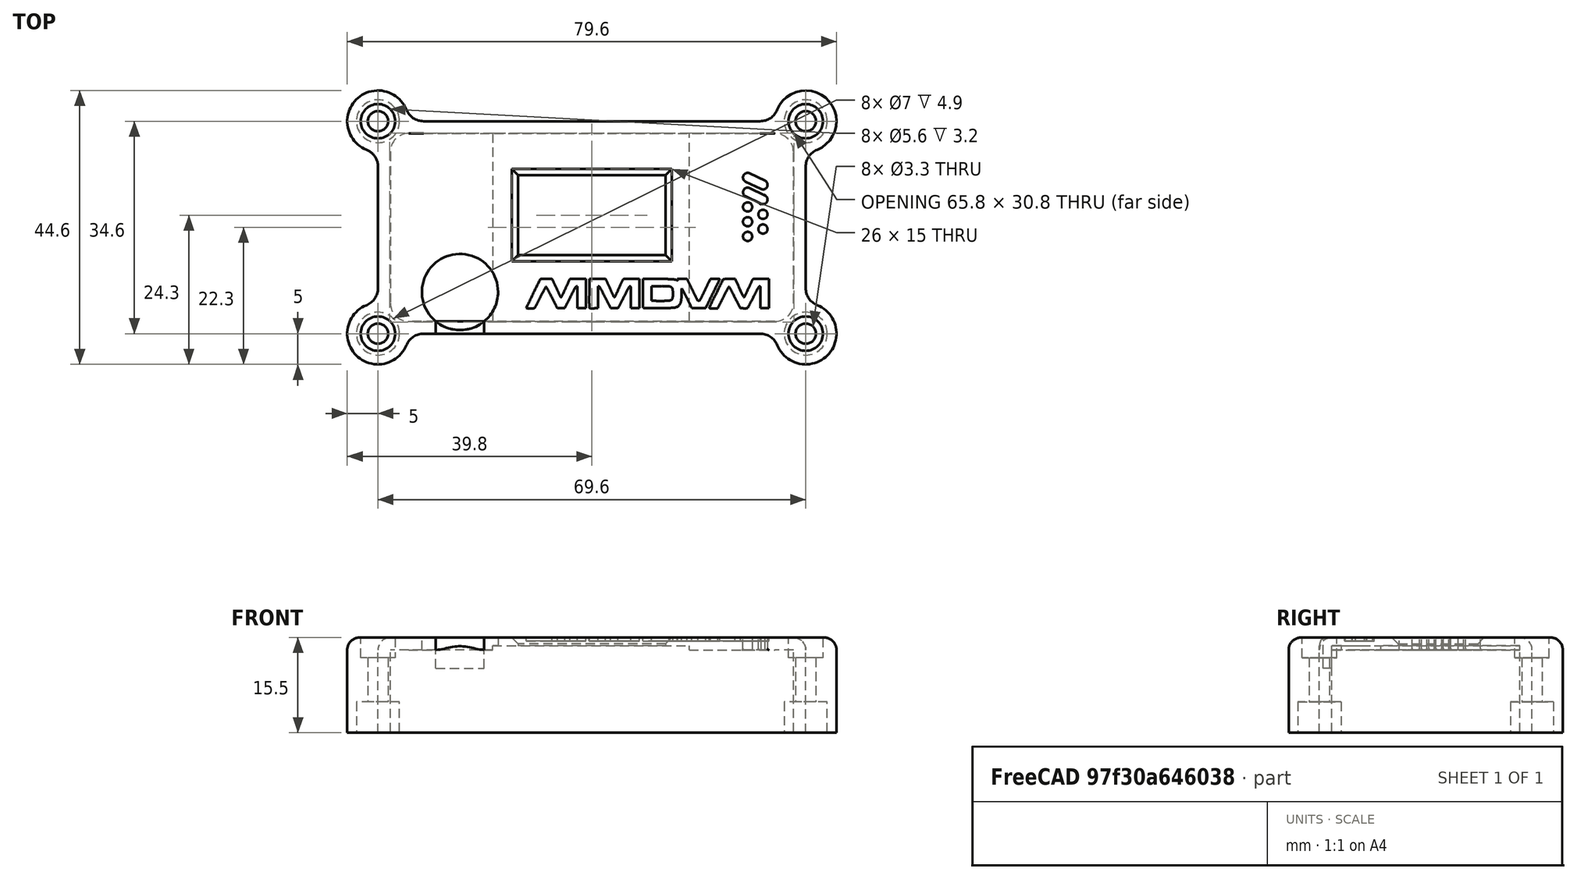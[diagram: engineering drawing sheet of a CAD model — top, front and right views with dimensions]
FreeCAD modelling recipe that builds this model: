
FCSTD DOCUMENT  (FreeCAD 0.18R13934 (Git))
Label: MMDVM_HS_Top-PCB-v1.6
License: CreativeCommons Attribution-NonCommercial-ShareAlike
LicenseURL: http://creativecommons.org/licenses/by-nc-sa/4.0/
objects: Sketcher::SketchObject×10, PartDesign::Pocket×6, Part::Feature×5, PartDesign::Fillet×4, Part::Cut×2, Part::FeaturePython×2, PartDesign::Pad×1, PartDesign::Chamfer×1, PartDesign::Hole×1, Part::MultiFuse×1, PartDesign::Body×1, Part::Extrusion×1, Mesh::Feature×1
note: 43 computed .brp shape members not serialized (recipe doc carries the construction recipe); baked Part::Feature solids carry a one-line shape summary decoded from their .brp

FEATURE [Sketcher::SketchObject] Sketch
  MapMode = 5
  Support = -> [XY_Plane]
  sketch-geometry (24):
    g0: LineSegment [constr] StartX=-32.5 StartY=15 StartZ=0 EndX=32.5 EndY=15 EndZ=0
    g1: LineSegment [constr] StartX=32.5 StartY=15 StartZ=0 EndX=32.5 EndY=-15 EndZ=0
    g2: LineSegment [constr] StartX=32.5 StartY=-15 StartZ=0 EndX=-32.5 EndY=-15 EndZ=0
    g3: LineSegment [constr] StartX=-32.5 StartY=-15 StartZ=0 EndX=-32.5 EndY=15 EndZ=0
    g4: LineSegment [constr] StartX=-29 StartY=11.5 StartZ=0 EndX=29 EndY=11.5 EndZ=0
    g5: LineSegment [constr] StartX=29 StartY=11.5 StartZ=0 EndX=29 EndY=-11.5 EndZ=0
    g6: LineSegment [constr] StartX=29 StartY=-11.5 StartZ=0 EndX=-29 EndY=-11.5 EndZ=0
    g7: LineSegment [constr] StartX=-29 StartY=-11.5 StartZ=0 EndX=-29 EndY=11.5 EndZ=0
    g8: Circle CenterX=-29 CenterY=11.5 CenterZ=0 NormalX=0 NormalY=0 NormalZ=1 AngleXU=0 Radius=1.375
    g9: Circle CenterX=29 CenterY=11.5 CenterZ=0 NormalX=0 NormalY=0 NormalZ=1 AngleXU=0 Radius=1.375
    g10: Circle CenterX=29 CenterY=-11.5 CenterZ=0 NormalX=0 NormalY=0 NormalZ=1 AngleXU=0 Radius=1.375
    g11: Circle CenterX=-29 CenterY=-11.5 CenterZ=0 NormalX=0 NormalY=0 NormalZ=1 AngleXU=0 Radius=1.375
    g12: LineSegment [constr] StartX=-29.5 StartY=12 StartZ=0 EndX=29.5 EndY=12 EndZ=0
    g13: LineSegment [constr] StartX=29.5 StartY=12 StartZ=0 EndX=29.5 EndY=-12 EndZ=0
    g14: LineSegment [constr] StartX=29.5 StartY=-12 StartZ=0 EndX=-29.5 EndY=-12 EndZ=0
    g15: LineSegment [constr] StartX=-29.5 StartY=-12 StartZ=0 EndX=-29.5 EndY=12 EndZ=0
    g16: ArcOfCircle CenterX=-29.5 CenterY=12 CenterZ=0 NormalX=0 NormalY=0 NormalZ=1 AngleXU=0 Radius=3 StartAngle=1.5708 EndAngle=3.1416
    g17: ArcOfCircle CenterX=29.5 CenterY=12 CenterZ=0 NormalX=0 NormalY=0 NormalZ=1 AngleXU=0 Radius=3 StartAngle=1.42077e-07 EndAngle=1.5708
    g18: ArcOfCircle CenterX=29.5 CenterY=-12 CenterZ=0 NormalX=0 NormalY=0 NormalZ=1 AngleXU=0 Radius=3 StartAngle=4.71239 EndAngle=6.28319
    g19: ArcOfCircle CenterX=-29.5 CenterY=-12 CenterZ=0 NormalX=0 NormalY=0 NormalZ=1 AngleXU=0 Radius=3 StartAngle=3.14159 EndAngle=4.71239
    g20: LineSegment StartX=-29.5 StartY=15 StartZ=0 EndX=29.5 EndY=15 EndZ=0
    g21: LineSegment StartX=32.5 StartY=12 StartZ=0 EndX=32.5 EndY=-12 EndZ=0
    g22: LineSegment StartX=29.5 StartY=-15 StartZ=0 EndX=-29.5 EndY=-15 EndZ=0
    g23: LineSegment StartX=-32.5 StartY=-12 StartZ=0 EndX=-32.5 EndY=12 EndZ=0
  constraints (68):
    c: Coincident(g0,g1)
    c: Coincident(g1,g2)
    c: Coincident(g2,g3)
    c: Coincident(g3,g0)
    c: Horizontal(g0)
    c: Horizontal(g2)
    c: Vertical(g1)
    c: Vertical(g3)
    c: DistanceX(g0,g0) = 65
    c: DistanceY(g1,g1) = 30
    c: Symmetric(g0,g0,g-2)
    c: Symmetric(g0,g1,g-1)
    c: Coincident(g4,g5)
    c: Coincident(g5,g6)
    c: Coincident(g6,g7)
    c: Coincident(g7,g4)
    c: Horizontal(g4)
    c: Horizontal(g6)
    c: Vertical(g5)
    c: Vertical(g7)
    c: DistanceX(g4,g4) = 58
    c: DistanceY(g5,g5) = 23
    c: Symmetric(g4,g5,g-1)
    c: Symmetric(g4,g4,g-2)
    c: Coincident(g8,g4)
    c: Coincident(g9,g4)
    c: Coincident(g10,g5)
    c: Coincident(g11,g6)
    c: Radius(g11) = 1.375
    c: Radius(g8) = 1.375
    c: Radius(g9) = 1.375
    c: Radius(g10) = 1.375
    c: Coincident(g12,g13)
    c: Coincident(g13,g14)
    c: Coincident(g14,g15)
    c: Coincident(g15,g12)
    c: Horizontal(g12)
    c: Horizontal(g14)
    c: Vertical(g13)
    c: Vertical(g15)
    c: DistanceX(g4,g12) = 0.5
    c: DistanceY(g4,g12) = 0.5
    c: DistanceY(g13,g5) = 0.5
    c: DistanceX(g14,g6) = 0.5
    c: Coincident(g16,g12)
    c: Radius(g16) = 3
    c: Coincident(g17,g12)
    c: Radius(g17) = 3
    c: Coincident(g18,g13)
    c: Radius(g18) = 3
    c: Coincident(g19,g14)
    c: Radius(g19) = 3
    c: PointOnObject(g16,g0)
    c: PointOnObject(g17,g1)
    c: PointOnObject(g18,g2)
    c: PointOnObject(g19,g3)
    c: Coincident(g20,g16)
    c: Horizontal(g20)
    c: Coincident(g20,g17)
    c: Coincident(g21,g17)
    c: Vertical(g21)
    c: Coincident(g18,g21)
    c: Coincident(g22,g18)
    c: Horizontal(g22)
    c: Coincident(g19,g22)
    c: Coincident(g23,g19)
    c: Vertical(g23)
    c: Coincident(g23,g16)
FEATURE [Sketcher::SketchObject] Sketch001
  MapMode = 5
  Support = -> [XY_Plane]
  expr: Constraints[8] = Sketch.Constraints[8]
  expr: Constraints[41] = Sketch.Constraints[41]
  expr: Constraints[9] = Sketch.Constraints[9]
  expr: Constraints[45] = Sketch.Constraints[45]
  expr: Constraints[43] = Sketch.Constraints[43]
  expr: Constraints[42] = Sketch.Constraints[42]
  expr: Constraints[20] = Sketch.Constraints[20]
  expr: Constraints[21] = Sketch.Constraints[21]
  expr: Constraints[28] = Sketch.Constraints[28]
  expr: Constraints[29] = Sketch.Constraints[29]
  expr: Constraints[30] = Sketch.Constraints[30]
  expr: Constraints[40] = Sketch.Constraints[40]
  expr: Constraints[31] = Sketch.Constraints[31]
  expr: Constraints[47] = Sketch.Constraints[47]
  expr: Constraints[49] = Sketch.Constraints[49]
  expr: Constraints[51] = Sketch.Constraints[51]
  sketch-geometry (64):
    g0: LineSegment [constr] StartX=-32.5 StartY=15 StartZ=0 EndX=32.5 EndY=15 EndZ=0
    g1: LineSegment [constr] StartX=32.5 StartY=15 StartZ=0 EndX=32.5 EndY=-15 EndZ=0
    g2: LineSegment [constr] StartX=32.5 StartY=-15 StartZ=0 EndX=-32.5 EndY=-15 EndZ=0
    g3: LineSegment [constr] StartX=-32.5 StartY=-15 StartZ=0 EndX=-32.5 EndY=15 EndZ=0
    g4: LineSegment [constr] StartX=-29 StartY=11.5 StartZ=0 EndX=29 EndY=11.5 EndZ=0
    g5: LineSegment [constr] StartX=29 StartY=11.5 StartZ=0 EndX=29 EndY=-11.5 EndZ=0
    g6: LineSegment [constr] StartX=29 StartY=-11.5 StartZ=0 EndX=-29 EndY=-11.5 EndZ=0
    g7: LineSegment [constr] StartX=-29 StartY=-11.5 StartZ=0 EndX=-29 EndY=11.5 EndZ=0
    g8: Circle [constr] CenterX=-29 CenterY=11.5 CenterZ=0 NormalX=0 NormalY=0 NormalZ=1 AngleXU=0 Radius=1.375
    g9: Circle [constr] CenterX=29 CenterY=11.5 CenterZ=0 NormalX=0 NormalY=0 NormalZ=1 AngleXU=0 Radius=1.375
    g10: Circle [constr] CenterX=29 CenterY=-11.5 CenterZ=0 NormalX=0 NormalY=0 NormalZ=1 AngleXU=0 Radius=1.375
    g11: Circle [constr] CenterX=-29 CenterY=-11.5 CenterZ=0 NormalX=0 NormalY=0 NormalZ=1 AngleXU=0 Radius=1.375
    g12: LineSegment [constr] StartX=-29.5 StartY=12 StartZ=0 EndX=29.5 EndY=12 EndZ=0
    g13: LineSegment [constr] StartX=29.5 StartY=12 StartZ=0 EndX=29.5 EndY=-12 EndZ=0
    g14: LineSegment [constr] StartX=29.5 StartY=-12 StartZ=0 EndX=-29.5 EndY=-12 EndZ=0
    g15: LineSegment [constr] StartX=-29.5 StartY=-12 StartZ=0 EndX=-29.5 EndY=12 EndZ=0
    g16: ArcOfCircle [constr] CenterX=-29.5 CenterY=12 CenterZ=0 NormalX=0 NormalY=0 NormalZ=1 AngleXU=0 Radius=3 StartAngle=1.5708 EndAngle=3.14159
    g17: ArcOfCircle [constr] CenterX=29.5 CenterY=12 CenterZ=0 NormalX=0 NormalY=0 NormalZ=1 AngleXU=0 Radius=3 StartAngle=2.8425e-08 EndAngle=1.5708
    g18: ArcOfCircle [constr] CenterX=29.5 CenterY=-12 CenterZ=0 NormalX=0 NormalY=0 NormalZ=1 AngleXU=0 Radius=3 StartAngle=4.71239 EndAngle=6.28319
    g19: ArcOfCircle [constr] CenterX=-29.5 CenterY=-12 CenterZ=0 NormalX=0 NormalY=0 NormalZ=1 AngleXU=0 Radius=3 StartAngle=3.14159 EndAngle=4.71239
    g20: LineSegment [constr] StartX=-29.5 StartY=15 StartZ=0 EndX=29.5 EndY=15 EndZ=0
    g21: LineSegment [constr] StartX=32.5 StartY=12 StartZ=0 EndX=32.5 EndY=-12 EndZ=0
    g22: LineSegment [constr] StartX=29.5 StartY=-15 StartZ=0 EndX=-29.5 EndY=-15 EndZ=0
    g23: LineSegment [constr] StartX=-32.5 StartY=-12 StartZ=0 EndX=-32.5 EndY=12 EndZ=0
    g24: ArcOfCircle [constr] CenterX=-29.5 CenterY=12 CenterZ=0 NormalX=0 NormalY=0 NormalZ=1 AngleXU=0 Radius=3.3 StartAngle=1.5708 EndAngle=3.14159
    g25: ArcOfCircle [constr] CenterX=29.5 CenterY=12 CenterZ=0 NormalX=0 NormalY=0 NormalZ=1 AngleXU=0 Radius=3.3 StartAngle=-2.2e-10 EndAngle=1.5708
    g26: ArcOfCircle [constr] CenterX=29.5 CenterY=-12 CenterZ=0 NormalX=0 NormalY=0 NormalZ=1 AngleXU=0 Radius=3.3 StartAngle=4.71239 EndAngle=6.28319
    g27: ArcOfCircle [constr] CenterX=-29.5 CenterY=-12 CenterZ=0 NormalX=0 NormalY=0 NormalZ=1 AngleXU=0 Radius=3.3 StartAngle=3.14159 EndAngle=4.71239
    g28: LineSegment [constr] StartX=-32.8 StartY=12 StartZ=0 EndX=-32.8 EndY=-12 EndZ=0
    g29: LineSegment [constr] StartX=-29.5 StartY=15.3 StartZ=0 EndX=29.5 EndY=15.3 EndZ=0
    g30: LineSegment [constr] StartX=32.8 StartY=12 StartZ=0 EndX=32.8 EndY=-12 EndZ=0
    g31: LineSegment [constr] StartX=29.5 StartY=-15.3 StartZ=0 EndX=-29.5 EndY=-15.3 EndZ=0
    g32: LineSegment [constr] StartX=-34.8 StartY=17.3 StartZ=0 EndX=34.8 EndY=17.3 EndZ=0
    g33: LineSegment [constr] StartX=34.8 StartY=17.3 StartZ=0 EndX=34.8 EndY=-17.3 EndZ=0
    g34: LineSegment [constr] StartX=34.8 StartY=-17.3 StartZ=0 EndX=-34.8 EndY=-17.3 EndZ=0
    g35: LineSegment [constr] StartX=-34.8 StartY=-17.3 StartZ=0 EndX=-34.8 EndY=17.3 EndZ=0
    g36: Circle [constr] CenterX=34.8 CenterY=17.3 CenterZ=0 NormalX=0 NormalY=0 NormalZ=1 AngleXU=0 Radius=5
    g37: Circle [constr] CenterX=34.8 CenterY=-17.3 CenterZ=0 NormalX=0 NormalY=0 NormalZ=1 AngleXU=0 Radius=5
    g38: Circle [constr] CenterX=-34.8 CenterY=-17.3 CenterZ=0 NormalX=0 NormalY=0 NormalZ=1 AngleXU=0 Radius=5
    g39: Circle [constr] CenterX=-34.8 CenterY=17.3 CenterZ=0 NormalX=0 NormalY=0 NormalZ=1 AngleXU=0 Radius=5
    g40: Circle [constr] CenterX=27.3838 CenterY=20.3 CenterZ=0 NormalX=0 NormalY=0 NormalZ=1 AngleXU=0 Radius=3
    g41: Circle [constr] CenterX=-27.3838 CenterY=20.3 CenterZ=0 NormalX=0 NormalY=0 NormalZ=1 AngleXU=0 Radius=3
    g42: Circle [constr] CenterX=-37.8 CenterY=9.8838 CenterZ=0 NormalX=0 NormalY=0 NormalZ=1 AngleXU=0 Radius=3
    g43: Circle [constr] CenterX=-37.8 CenterY=-9.8838 CenterZ=0 NormalX=0 NormalY=0 NormalZ=1 AngleXU=0 Radius=3
    g44: Circle [constr] CenterX=-27.3838 CenterY=-20.3 CenterZ=0 NormalX=0 NormalY=0 NormalZ=1 AngleXU=0 Radius=3
    g45: Circle [constr] CenterX=27.3838 CenterY=-20.3 CenterZ=0 NormalX=0 NormalY=0 NormalZ=1 AngleXU=0 Radius=3
    g46: Circle [constr] CenterX=37.8 CenterY=-9.8838 CenterZ=0 NormalX=0 NormalY=0 NormalZ=1 AngleXU=0 Radius=3
    g47: Circle [constr] CenterX=37.8 CenterY=9.8838 CenterZ=0 NormalX=0 NormalY=0 NormalZ=1 AngleXU=0 Radius=3
    g48: ArcOfCircle CenterX=34.8 CenterY=17.3 CenterZ=0 NormalX=0 NormalY=0 NormalZ=1 AngleXU=0 Radius=5 StartAngle=5.09679 EndAngle=9.04038
    g49: ArcOfCircle CenterX=27.3838 CenterY=20.3 CenterZ=0 NormalX=0 NormalY=0 NormalZ=1 AngleXU=0 Radius=3 StartAngle=4.71239 EndAngle=5.89879
    g50: ArcOfCircle CenterX=37.8 CenterY=9.8838 CenterZ=0 NormalX=0 NormalY=0 NormalZ=1 AngleXU=0 Radius=3 StartAngle=1.95519 EndAngle=3.14159
    g51: ArcOfCircle CenterX=37.8 CenterY=-9.8838 CenterZ=0 NormalX=0 NormalY=0 NormalZ=1 AngleXU=0 Radius=3 StartAngle=3.14159 EndAngle=4.32799
    g52: ArcOfCircle CenterX=34.8 CenterY=-17.3 CenterZ=0 NormalX=0 NormalY=0 NormalZ=1 AngleXU=0 Radius=5 StartAngle=3.52599 EndAngle=7.46958
    g53: ArcOfCircle CenterX=27.3838 CenterY=-20.3 CenterZ=0 NormalX=0 NormalY=0 NormalZ=1 AngleXU=0 Radius=3 StartAngle=0.384397 EndAngle=1.5708
    g54: ArcOfCircle CenterX=-27.3838 CenterY=-20.3 CenterZ=0 NormalX=0 NormalY=0 NormalZ=1 AngleXU=0 Radius=3 StartAngle=1.5708 EndAngle=2.7572
    g55: ArcOfCircle CenterX=-34.8 CenterY=-17.3 CenterZ=0 NormalX=0 NormalY=0 NormalZ=1 AngleXU=0 Radius=5 StartAngle=1.95519 EndAngle=5.89879
    g56: ArcOfCircle CenterX=-37.8 CenterY=-9.8838 CenterZ=0 NormalX=0 NormalY=0 NormalZ=1 AngleXU=0 Radius=3 StartAngle=5.09679 EndAngle=6.28319
    g57: ArcOfCircle CenterX=-37.8 CenterY=9.8838 CenterZ=0 NormalX=0 NormalY=0 NormalZ=1 AngleXU=0 Radius=3 StartAngle=6.28319 EndAngle=7.46958
    g58: ArcOfCircle CenterX=-34.8 CenterY=17.3 CenterZ=0 NormalX=0 NormalY=0 NormalZ=1 AngleXU=0 Radius=5 StartAngle=0.384397 EndAngle=4.32799
    g59: ArcOfCircle CenterX=-27.3838 CenterY=20.3 CenterZ=0 NormalX=0 NormalY=0 NormalZ=1 AngleXU=0 Radius=3 StartAngle=3.52599 EndAngle=4.71239
    g60: LineSegment StartX=-27.3838 StartY=17.3 StartZ=0 EndX=27.3838 EndY=17.3 EndZ=0
    g61: LineSegment StartX=34.8 StartY=9.8838 StartZ=0 EndX=34.8 EndY=-9.8838 EndZ=0
    g62: LineSegment StartX=27.3838 StartY=-17.3 StartZ=0 EndX=-27.3838 EndY=-17.3 EndZ=0
    g63: LineSegment StartX=-34.8 StartY=-9.8838 StartZ=0 EndX=-34.8 EndY=9.8838 EndZ=0
  constraints (184):
    c: Coincident(g0,g1)
    c: Coincident(g1,g2)
    c: Coincident(g2,g3)
    c: Coincident(g3,g0)
    c: Horizontal(g0)
    c: Horizontal(g2)
    c: Vertical(g1)
    c: Vertical(g3)
    c: DistanceX(g0,g0) = 65
    c: DistanceY(g1,g1) = 30
    c: Symmetric(g0,g0,g-2)
    c: Symmetric(g0,g1,g-1)
    c: Coincident(g4,g5)
    c: Coincident(g5,g6)
    c: Coincident(g6,g7)
    c: Coincident(g7,g4)
    c: Horizontal(g4)
    c: Horizontal(g6)
    c: Vertical(g5)
    c: Vertical(g7)
    c: DistanceX(g4,g4) = 58
    c: DistanceY(g5,g5) = 23
    c: Symmetric(g4,g5,g-1)
    c: Symmetric(g4,g4,g-2)
    c: Coincident(g8,g4)
    c: Coincident(g9,g4)
    c: Coincident(g10,g5)
    c: Coincident(g11,g6)
    c: Radius(g11) = 1.375
    c: Radius(g8) = 1.375
    c: Radius(g9) = 1.375
    c: Radius(g10) = 1.375
    c: Coincident(g12,g13)
    c: Coincident(g13,g14)
    c: Coincident(g14,g15)
    c: Coincident(g15,g12)
    c: Horizontal(g12)
    c: Horizontal(g14)
    c: Vertical(g13)
    c: Vertical(g15)
    c: DistanceX(g4,g12) = 0.5
    c: DistanceY(g4,g12) = 0.5
    c: DistanceY(g13,g5) = 0.5
    c: DistanceX(g14,g6) = 0.5
    c: Coincident(g16,g12)
    c: Radius(g16) = 3
    c: Coincident(g17,g12)
    c: Radius(g17) = 3
    c: Coincident(g18,g13)
    c: Radius(g18) = 3
    c: Coincident(g19,g14)
    c: Radius(g19) = 3
    c: PointOnObject(g16,g0)
    c: PointOnObject(g17,g1)
    c: PointOnObject(g18,g2)
    c: PointOnObject(g19,g3)
    c: Coincident(g20,g16)
    c: Horizontal(g20)
    c: Coincident(g20,g17)
    c: Coincident(g21,g17)
    c: Vertical(g21)
    c: Coincident(g18,g21)
    c: Coincident(g22,g18)
    c: Horizontal(g22)
    c: Coincident(g19,g22)
    c: Coincident(g23,g19)
    c: Vertical(g23)
    c: Coincident(g23,g16)
    c: Coincident(g24,g12)
    c: Radius(g24) = 3.3
    c: Coincident(g25,g12)
    c: Radius(g25) = 3.3
    c: Coincident(g26,g13)
    c: Radius(g26) = 3.3
    c: Coincident(g27,g14)
    c: Radius(g27) = 3.3
    c: Vertical(g28)
    c: DistanceX(g28,g2) = 0.3
    c: Coincident(g27,g28)
    c: Coincident(g28,g24)
    c: Horizontal(g29)
    c: DistanceY(g0,g29) = 0.3
    c: Coincident(g24,g29)
    c: Coincident(g25,g29)
    c: Vertical(g30)
    c: DistanceX(g0,g30) = 0.3
    c: Coincident(g25,g30)
    c: Coincident(g30,g26)
    c: Horizontal(g31)
    c: DistanceY(g31,g1) = 0.3
    c: Coincident(g31,g26)
    c: Coincident(g31,g27)
    c: Coincident(g32,g33)
    c: Coincident(g33,g34)
    c: Coincident(g34,g35)
    c: Coincident(g35,g32)
    c: Horizontal(g32)
    c: Horizontal(g34)
    c: Vertical(g33)
    c: Vertical(g35)
    c: DistanceY(g25,g32) = 2
    c: DistanceX(g25,g32) = 2
    c: DistanceY(g33,g26) = 2
    c: DistanceX(g34,g27) = 2
    c: Coincident(g36,g32)
    c: Coincident(g37,g33)
    c: Coincident(g38,g34)
    c: Coincident(g39,g32)
    c: Radius(g39) = 5
    c: Radius(g38) = 5
    c: Radius(g37) = 5
    c: Radius(g36) = 5
    c: Radius(g40) = 3
    c: Tangent(g40,g36)
    c: Tangent(g40,g32)
    c: Tangent(g47,g36)
    c: Radius(g47) = 3
    c: Tangent(g47,g33)
    c: Radius(g46) = 3
    c: Tangent(g46,g37)
    c: Tangent(g46,g33)
    c: Radius(g45) = 3
    c: Tangent(g45,g37)
    c: Tangent(g45,g34)
    c: Radius(g44) = 3
    c: Tangent(g44,g34)
    c: Tangent(g44,g38)
    c: Radius(g43) = 3
    c: Tangent(g43,g38)
    c: Tangent(g43,g35)
    c: Radius(g42) = 3
    c: Tangent(g42,g35)
    c: Tangent(g42,g39)
    c: Radius(g41) = 3
    c: Tangent(g41,g32)
    c: Tangent(g41,g39)
    c: Coincident(g48,g32)
    c: PointOnObject(g48,g36)
    c: Coincident(g49,g40)
    c: PointOnObject(g49,g40)
    c: Coincident(g50,g47)
    c: PointOnObject(g50,g47)
    c: Coincident(g51,g46)
    c: PointOnObject(g51,g46)
    c: Coincident(g52,g33)
    c: PointOnObject(g52,g37)
    c: Coincident(g53,g45)
    c: PointOnObject(g53,g45)
    c: Coincident(g54,g44)
    c: PointOnObject(g54,g44)
    c: Coincident(g55,g34)
    c: PointOnObject(g55,g38)
    c: Coincident(g56,g43)
    c: PointOnObject(g56,g43)
    c: Coincident(g57,g42)
    c: PointOnObject(g57,g42)
    c: Coincident(g58,g32)
    c: PointOnObject(g58,g39)
    c: Coincident(g59,g41)
    c: PointOnObject(g59,g41)
    c: Coincident(g49,g48)
    c: Coincident(g48,g50)
    c: Coincident(g51,g52)
    c: Coincident(g52,g53)
    c: Coincident(g54,g55)
    c: Coincident(g55,g56)
    c: Coincident(g57,g58)
    c: Coincident(g58,g59)
    c: PointOnObject(g60,g32)
    c: Horizontal(g60)
    c: PointOnObject(g61,g33)
    c: Vertical(g61)
    c: PointOnObject(g62,g34)
    c: Horizontal(g62)
    c: PointOnObject(g63,g35)
    c: Vertical(g63)
    c: Coincident(g59,g60)
    c: Coincident(g60,g49)
    c: Coincident(g50,g61)
    c: Coincident(g61,g51)
    c: Coincident(g53,g62)
    c: Coincident(g54,g62)
    c: Coincident(g56,g63)
    c: Coincident(g57,g63)
FEATURE [PartDesign::Pad] Pad
  Length = 15.5
  Length2 = 100
  Profile = -> Sketch001
  Type = 0
FEATURE [Sketcher::SketchObject] Sketch002
  ExternalGeometry = -> [Pad]
  MapMode = 5
  Placement = pos=(0,0,0) rot=(1,0,0;3.14159rad)
  Support = -> [Pad]
  sketch-geometry (4):
    g0: Circle CenterX=34.8 CenterY=17.3 CenterZ=0 NormalX=0 NormalY=0 NormalZ=1 AngleXU=0 Radius=3.5
    g1: Circle CenterX=34.8 CenterY=-17.3 CenterZ=0 NormalX=0 NormalY=0 NormalZ=1 AngleXU=0 Radius=3.5
    g2: Circle CenterX=-34.8 CenterY=-17.3 CenterZ=0 NormalX=0 NormalY=0 NormalZ=1 AngleXU=0 Radius=3.5
    g3: Circle CenterX=-34.8 CenterY=17.3 CenterZ=0 NormalX=0 NormalY=0 NormalZ=1 AngleXU=0 Radius=3.5
  constraints (8):
    c: Coincident(g0,g-3)
    c: Radius(g0) = 3.5
    c: Coincident(g1,g-6)
    c: Radius(g1) = 3.5
    c: Coincident(g2,g-5)
    c: Radius(g2) = 3.5
    c: Coincident(g3,g-4)
    c: Radius(g3) = 3.5
FEATURE [PartDesign::Pocket] Pocket
  BaseFeature = -> Pad
  Length = 5
  Length2 = 100
  Profile = -> Sketch002
  Type = 0
FEATURE [Sketcher::SketchObject] Sketch003
  MapMode = 5
  Placement = pos=(0,0,0) rot=(1,0,0;3.14159rad)
  Support = -> [Pocket]
  expr: Constraints[8] = Sketch.Constraints[8]
  expr: Constraints[39] = Sketch.Constraints[40]
  expr: Constraints[30] = Sketch.Constraints[31]
  expr: Constraints[27] = Sketch.Constraints[28]
  expr: Constraints[29] = Sketch.Constraints[30]
  expr: Constraints[28] = Sketch.Constraints[29]
  expr: Constraints[20] = -Sketch.Constraints[21]
  expr: Constraints[19] = Sketch.Constraints[20]
  expr: Constraints[42] = Sketch.Constraints[43]
  expr: Constraints[41] = -Sketch.Constraints[42]
  expr: Constraints[9] = -Sketch.Constraints[9]
  expr: Constraints[40] = -Sketch.Constraints[41]
  sketch-geometry (32):
    g0: LineSegment [constr] StartX=-32.5 StartY=-15 StartZ=0 EndX=32.5 EndY=-15 EndZ=0
    g1: LineSegment [constr] StartX=32.5 StartY=-15 StartZ=0 EndX=32.5 EndY=15 EndZ=0
    g2: LineSegment [constr] StartX=32.5 StartY=15 StartZ=0 EndX=-32.5 EndY=15 EndZ=0
    g3: LineSegment [constr] StartX=-32.5 StartY=15 StartZ=0 EndX=-32.5 EndY=-15 EndZ=0
    g4: LineSegment [constr] StartX=-29 StartY=-11.5 StartZ=0 EndX=29 EndY=-11.5 EndZ=0
    g5: LineSegment [constr] StartX=29 StartY=-11.5 StartZ=0 EndX=29 EndY=11.5 EndZ=0
    g6: LineSegment [constr] StartX=29 StartY=11.5 StartZ=0 EndX=-29 EndY=11.5 EndZ=0
    g7: LineSegment [constr] StartX=-29 StartY=11.5 StartZ=0 EndX=-29 EndY=-11.5 EndZ=0
    g8: Circle [constr] CenterX=-29 CenterY=-11.5 CenterZ=0 NormalX=0 NormalY=0 NormalZ=1 AngleXU=0 Radius=1.375
    g9: Circle [constr] CenterX=29 CenterY=-11.5 CenterZ=0 NormalX=0 NormalY=0 NormalZ=1 AngleXU=0 Radius=1.375
    g10: Circle [constr] CenterX=29 CenterY=11.5 CenterZ=0 NormalX=0 NormalY=0 NormalZ=1 AngleXU=0 Radius=1.375
    g11: Circle [constr] CenterX=-29 CenterY=11.5 CenterZ=0 NormalX=0 NormalY=0 NormalZ=1 AngleXU=0 Radius=1.375
    g12: LineSegment [constr] StartX=-29.5 StartY=-12 StartZ=0 EndX=29.5 EndY=-12 EndZ=0
    g13: LineSegment [constr] StartX=29.5 StartY=-12 StartZ=0 EndX=29.5 EndY=12 EndZ=0
    g14: LineSegment [constr] StartX=29.5 StartY=12 StartZ=0 EndX=-29.5 EndY=12 EndZ=0
    g15: LineSegment [constr] StartX=-29.5 StartY=12 StartZ=0 EndX=-29.5 EndY=-12 EndZ=0
    g16: LineSegment [constr] StartX=-29.5121 StartY=-15 StartZ=0 EndX=29.5 EndY=-15 EndZ=0
    g17: LineSegment [constr] StartX=32.5 StartY=-12 StartZ=0 EndX=32.5 EndY=12 EndZ=0
    g18: LineSegment [constr] StartX=29.5 StartY=15 StartZ=0 EndX=-29.5121 EndY=15 EndZ=0
    g19: LineSegment [constr] StartX=-32.5 StartY=12 StartZ=0 EndX=-32.5 EndY=-12 EndZ=0
    g20: ArcOfCircle [constr] CenterX=-29.5 CenterY=12 CenterZ=0 NormalX=0 NormalY=0 NormalZ=1 AngleXU=0 Radius=3.00002 StartAngle=1.57483 EndAngle=3.1416
    g21: ArcOfCircle [constr] CenterX=29.5 CenterY=12 CenterZ=0 NormalX=0 NormalY=0 NormalZ=1 AngleXU=0 Radius=3 StartAngle=6.28318 EndAngle=7.85399
    g22: ArcOfCircle [constr] CenterX=29.5 CenterY=-12 CenterZ=0 NormalX=0 NormalY=0 NormalZ=1 AngleXU=0 Radius=3 StartAngle=4.71238 EndAngle=6.28319
    g23: ArcOfCircle [constr] CenterX=-29.5 CenterY=-12 CenterZ=0 NormalX=0 NormalY=0 NormalZ=1 AngleXU=0 Radius=3.00002 StartAngle=3.14159 EndAngle=4.70836
    g24: LineSegment StartX=-29.8 StartY=15.3 StartZ=0 EndX=29.8 EndY=15.3 EndZ=0
    g25: LineSegment StartX=32.8 StartY=12.3 StartZ=0 EndX=32.8 EndY=-12.3 EndZ=0
    g26: LineSegment StartX=29.8 StartY=-15.3 StartZ=0 EndX=-29.8 EndY=-15.3 EndZ=0
    g27: LineSegment StartX=-32.8 StartY=-12.3 StartZ=0 EndX=-32.8 EndY=12.3 EndZ=0
    g28: ArcOfCircle CenterX=29.8 CenterY=12.3 CenterZ=0 NormalX=0 NormalY=0 NormalZ=1 AngleXU=0 Radius=3 StartAngle=0 EndAngle=1.5708
    g29: ArcOfCircle CenterX=29.8 CenterY=-12.3 CenterZ=0 NormalX=0 NormalY=0 NormalZ=1 AngleXU=0 Radius=3 StartAngle=4.71239 EndAngle=6.28319
    g30: ArcOfCircle CenterX=-29.8 CenterY=-12.3 CenterZ=0 NormalX=0 NormalY=0 NormalZ=1 AngleXU=0 Radius=3 StartAngle=3.14159 EndAngle=4.71239
    g31: ArcOfCircle CenterX=-29.8 CenterY=12.3 CenterZ=0 NormalX=0 NormalY=0 NormalZ=1 AngleXU=0 Radius=3 StartAngle=1.5708 EndAngle=3.14159
  constraints (83):
    c: Coincident(g0,g1)
    c: Coincident(g1,g2)
    c: Coincident(g2,g3)
    c: Coincident(g3,g0)
    c: Horizontal(g0)
    c: Horizontal(g2)
    c: Vertical(g1)
    c: Vertical(g3)
    c: DistanceX(g0,g0) = 65
    c: DistanceY(g1,g1) = -30
    c: Symmetric(g0,g0,g-2)
    c: Symmetric(g0,g1,g-1)
    c: Coincident(g4,g5)
    c: Coincident(g5,g6)
    c: Coincident(g6,g7)
    c: Horizontal(g4)
    c: Horizontal(g6)
    c: Vertical(g5)
    c: Vertical(g7)
    c: DistanceX(g4,g4) = 58
    c: DistanceY(g5,g5) = -23
    c: Symmetric(g4,g5,g-1)
    c: Symmetric(g4,g4,g-2)
    c: Coincident(g8,g4)
    c: Coincident(g9,g4)
    c: Coincident(g10,g5)
    c: Coincident(g11,g6)
    c: Radius(g11) = 1.375
    c: Radius(g8) = 1.375
    c: Radius(g9) = 1.375
    c: Radius(g10) = 1.375
    c: Coincident(g12,g13)
    c: Coincident(g13,g14)
    c: Coincident(g14,g15)
    c: Coincident(g15,g12)
    c: Horizontal(g12)
    c: Horizontal(g14)
    c: Vertical(g13)
    c: Vertical(g15)
    c: DistanceX(g4,g12) = 0.5
    c: DistanceY(g4,g12) = -0.5
    c: DistanceY(g13,g5) = -0.5
    c: DistanceX(g14,g6) = 0.5
    c: PointOnObject(g16,g0)
    c: PointOnObject(g17,g1)
    c: PointOnObject(g18,g2)
    c: PointOnObject(g19,g3)
    c: Horizontal(g16)
    c: Vertical(g17)
    c: Horizontal(g18)
    c: Vertical(g19)
    c: Coincident(g20,g14)
    c: Coincident(g20,g18)
    c: Coincident(g20,g19)
    c: Coincident(g21,g13)
    c: Coincident(g21,g17)
    c: Coincident(g21,g18)
    c: Coincident(g22,g12)
    c: Coincident(g22,g16)
    c: Coincident(g22,g17)
    c: Coincident(g23,g12)
    c: Coincident(g23,g19)
    c: Coincident(g23,g16)
    c: Horizontal(g24)
    c: Horizontal(g26)
    c: Vertical(g25)
    c: Vertical(g27)
    c: Tangent(g24,g28) = 1.5708
    c: Tangent(g25,g28) = 1.5708
    c: Tangent(g25,g29) = 1.5708
    c: Tangent(g26,g29) = 1.5708
    c: Tangent(g26,g30) = 1.5708
    c: Tangent(g27,g30) = 1.5708
    c: Tangent(g27,g31) = 1.5708
    c: Tangent(g24,g31) = 1.5708
    c: Radius(g31) = 3
    c: Radius(g28) = 3
    c: Radius(g29) = 3
    c: Radius(g30) = 3
    c: DistanceY(g1,g24) = 0.3
    c: DistanceX(g17,g25) = 0.3
    c: DistanceY(g26,g16) = 0.3
    c: DistanceX(g27,g19) = 0.3
FEATURE [PartDesign::Pocket] Pocket001
  BaseFeature = -> Pocket
  Length = 13.5
  Length2 = 100
  Profile = -> Sketch003
  Type = 0
FEATURE [Sketcher::SketchObject] Sketch004
  ExternalGeometry = -> [Pocket001]
  MapMode = 5
  Placement = pos=(0,0,15.5) rot=(0,0,1;0rad)
  Support = -> [Pocket001]
  sketch-geometry (32):
    g0: LineSegment StartX=-27.3838 StartY=17.3 StartZ=0 EndX=-31.8 EndY=17.3 EndZ=0
    g1: LineSegment StartX=-34.8 StartY=9.8838 StartZ=0 EndX=-34.8 EndY=14.3 EndZ=0
    g2: Circle [constr] CenterX=-31.8 CenterY=14.3 CenterZ=0 NormalX=0 NormalY=0 NormalZ=1 AngleXU=0 Radius=3
    g3: ArcOfCircle CenterX=-31.8 CenterY=14.3 CenterZ=0 NormalX=0 NormalY=0 NormalZ=1 AngleXU=0 Radius=3 StartAngle=1.5708 EndAngle=3.14159
    g4: LineSegment StartX=-41.7809 StartY=24.2149 StartZ=0 EndX=-27.3838 EndY=24.2149 EndZ=0
    g5: LineSegment StartX=-41.7809 StartY=9.8838 StartZ=0 EndX=-41.7809 EndY=24.2149 EndZ=0
    g6: LineSegment StartX=-27.3838 StartY=24.2149 StartZ=0 EndX=-27.3838 EndY=17.3 EndZ=0
    g7: LineSegment StartX=-41.7809 StartY=9.8838 StartZ=0 EndX=-34.8 EndY=9.8838 EndZ=0
    g8: LineSegment StartX=27.3838 StartY=17.3 StartZ=0 EndX=31.8 EndY=17.3 EndZ=0
    g9: LineSegment StartX=34.8 StartY=9.8838 StartZ=0 EndX=34.8 EndY=14.3 EndZ=0
    g10: Circle [constr] CenterX=31.8 CenterY=14.3 CenterZ=0 NormalX=0 NormalY=0 NormalZ=1 AngleXU=0 Radius=3
    g11: ArcOfCircle CenterX=31.8 CenterY=14.3 CenterZ=0 NormalX=0 NormalY=0 NormalZ=1 AngleXU=0 Radius=3 StartAngle=4.4834e-08 EndAngle=1.5708
    g12: LineSegment StartX=41.7622 StartY=24.6512 StartZ=0 EndX=27.3838 EndY=24.6512 EndZ=0
    g13: LineSegment StartX=41.7622 StartY=9.8838 StartZ=0 EndX=41.7622 EndY=24.6512 EndZ=0
    g14: LineSegment StartX=27.3838 StartY=24.6512 StartZ=0 EndX=27.3838 EndY=17.3 EndZ=0
    g15: LineSegment StartX=41.7622 StartY=9.8838 StartZ=0 EndX=34.8 EndY=9.8838 EndZ=0
    g16: LineSegment StartX=-34.8 StartY=-9.8838 StartZ=0 EndX=-34.8 EndY=-14.3 EndZ=0
    g17: LineSegment StartX=-27.3838 StartY=-17.3 StartZ=0 EndX=-31.8 EndY=-17.3 EndZ=0
    g18: Circle [constr] CenterX=-31.8 CenterY=-14.3 CenterZ=0 NormalX=0 NormalY=0 NormalZ=1 AngleXU=0 Radius=3
    g19: ArcOfCircle CenterX=-31.8 CenterY=-14.3 CenterZ=0 NormalX=0 NormalY=0 NormalZ=1 AngleXU=0 Radius=3 StartAngle=3.14159 EndAngle=4.71239
    g20: LineSegment StartX=-27.3838 StartY=-24.2044 StartZ=0 EndX=-41.4724 EndY=-24.2044 EndZ=0
    g21: LineSegment StartX=-41.4724 StartY=-24.2044 StartZ=0 EndX=-41.4724 EndY=-9.8838 EndZ=0
    g22: LineSegment StartX=-41.4724 StartY=-9.8838 StartZ=0 EndX=-34.8 EndY=-9.8838 EndZ=0
    g23: LineSegment StartX=-27.3838 StartY=-24.2044 StartZ=0 EndX=-27.3838 EndY=-17.3 EndZ=0
    g24: LineSegment StartX=34.8 StartY=-9.8838 StartZ=0 EndX=34.8 EndY=-14.3 EndZ=0
    g25: LineSegment StartX=27.3838 StartY=-17.3 StartZ=0 EndX=31.8 EndY=-17.3 EndZ=0
    g26: Circle [constr] CenterX=31.8 CenterY=-14.3 CenterZ=0 NormalX=0 NormalY=0 NormalZ=1 AngleXU=0 Radius=3
    g27: ArcOfCircle CenterX=31.8 CenterY=-14.3 CenterZ=0 NormalX=0 NormalY=0 NormalZ=1 AngleXU=0 Radius=3 StartAngle=4.71239 EndAngle=6.28319
    g28: LineSegment StartX=41.5436 StartY=-23.6904 StartZ=0 EndX=27.3838 EndY=-23.6904 EndZ=0
    g29: LineSegment StartX=41.5436 StartY=-9.8838 StartZ=0 EndX=41.5436 EndY=-23.6904 EndZ=0
    g30: LineSegment StartX=41.5436 StartY=-9.8838 StartZ=0 EndX=34.8 EndY=-9.8838 EndZ=0
    g31: LineSegment StartX=27.3838 StartY=-23.6904 StartZ=0 EndX=27.3838 EndY=-17.3 EndZ=0
  constraints (88):
    c: PointOnObject(g0,g-3)
    c: Horizontal(g0)
    c: PointOnObject(g1,g-6)
    c: Vertical(g1)
    c: Radius(g2) = 3
    c: Tangent(g2,g0)
    c: Tangent(g2,g1)
    c: Coincident(g3,g2)
    c: PointOnObject(g3,g2)
    c: Coincident(g3,g1)
    c: Coincident(g3,g0)
    c: Coincident(g5,g4)
    c: Horizontal(g4)
    c: Vertical(g5)
    c: Coincident(g6,g4)
    c: Vertical(g6)
    c: Coincident(g7,g5)
    c: Horizontal(g7)
    c: Coincident(g7,g1)
    c: Coincident(g6,g0)
    c: PointOnObject(g8,g-3)
    c: Horizontal(g8)
    c: PointOnObject(g9,g-4)
    c: Vertical(g9)
    c: Radius(g10) = 3
    c: Tangent(g10,g8)
    c: Tangent(g10,g9)
    c: Coincident(g11,g10)
    c: PointOnObject(g11,g10)
    c: Coincident(g11,g8)
    c: Coincident(g11,g9)
    c: Coincident(g13,g12)
    c: Horizontal(g12)
    c: Vertical(g13)
    c: Coincident(g14,g12)
    c: Vertical(g14)
    c: Coincident(g15,g13)
    c: Horizontal(g15)
    c: Coincident(g15,g9)
    c: Coincident(g14,g8)
    c: PointOnObject(g16,g-6)
    c: Vertical(g16)
    c: PointOnObject(g17,g-5)
    c: Horizontal(g17)
    c: Radius(g18) = 3
    c: Tangent(g18,g16)
    c: Tangent(g18,g17)
    c: Coincident(g19,g18)
    c: PointOnObject(g19,g18)
    c: Coincident(g19,g17)
    c: Coincident(g19,g16)
    c: Coincident(g20,g21)
    c: Horizontal(g20)
    c: Vertical(g21)
    c: Coincident(g22,g21)
    c: Horizontal(g22)
    c: Coincident(g23,g20)
    c: Vertical(g23)
    c: Coincident(g23,g17)
    c: Coincident(g22,g16)
    c: PointOnObject(g24,g-4)
    c: Vertical(g24)
    c: PointOnObject(g25,g-5)
    c: Horizontal(g25)
    c: Radius(g26) = 3
    c: Tangent(g26,g24)
    c: Tangent(g26,g25)
    c: Coincident(g27,g26)
    c: PointOnObject(g27,g26)
    c: Coincident(g27,g24)
    c: Coincident(g27,g25)
    c: Coincident(g29,g28)
    c: Horizontal(g28)
    c: Vertical(g29)
    c: Coincident(g30,g29)
    c: Horizontal(g30)
    c: Coincident(g31,g28)
    c: Vertical(g31)
    c: Coincident(g31,g25)
    c: Coincident(g30,g24)
    c: Coincident(g0,g-3)
    c: Coincident(g1,g-6)
    c: Coincident(g-6,g16)
    c: Coincident(g17,g-5)
    c: Coincident(g-5,g25)
    c: Coincident(g-4,g24)
    c: Coincident(g9,g-4)
    c: Coincident(g8,g-3)
FEATURE [Sketcher::SketchObject] Sketch005
  ExternalGeometry = -> [Pocket001,Sketch]
  MapMode = 5
  Placement = pos=(0,0,15.5) rot=(0,0,1;0rad)
  Support = -> [Pocket001]
  sketch-geometry (10):
    g0: LineSegment [constr] StartX=-21.4583 StartY=31.2328 StartZ=0 EndX=-21.4583 EndY=-27.0552 EndZ=0
    g1: LineSegment [constr] StartX=-45.4064 StartY=-10.5129 StartZ=0 EndX=40.4454 EndY=-10.5129 EndZ=0
    g2: Circle [constr] CenterX=-21.4583 CenterY=-10.5129 CenterZ=0 NormalX=0 NormalY=0 NormalZ=1 AngleXU=0 Radius=6.2
    g3: LineSegment StartX=-12 StartY=8.5 StartZ=0 EndX=12 EndY=8.5 EndZ=0
    g4: LineSegment StartX=12 StartY=8.5 StartZ=0 EndX=12 EndY=-4.5 EndZ=0
    g5: LineSegment StartX=12 StartY=-4.5 StartZ=0 EndX=-12 EndY=-4.5 EndZ=0
    g6: LineSegment StartX=-12 StartY=-4.5 StartZ=0 EndX=-12 EndY=8.5 EndZ=0
    g7: LineSegment [constr] StartX=-29 StartY=24.9491 StartZ=0 EndX=-29 EndY=-20.674 EndZ=0
    g8: LineSegment [constr] StartX=-44.8443 StartY=11.5 StartZ=0 EndX=14.9752 EndY=11.5 EndZ=0
    g9: Circle CenterX=-21.4583 CenterY=-10.5129 CenterZ=0 NormalX=0 NormalY=0 NormalZ=1 AngleXU=0 Radius=6.2
  constraints (26):
    c: Coincident(g5,g6)
    c: Coincident(g3,g6)
    c: Coincident(g4,g5)
    c: Coincident(g3,g4)
    c: DistanceX(g3,g3) = 24
    c: DistanceY(g4,g4) = 13
    c: Vertical(g7)
    c: Horizontal(g8)
    c: PointOnObject(g-4,g8)
    c: PointOnObject(g-4,g7)
    c: PointOnObject(g2,g0)
    c: PointOnObject(g2,g1)
    c: DistanceX(g7,g0) = 7.54172
    c: DistanceX(g7,g3) = 17
    c: DistanceY(g3,g-4) = 3
    c: DistanceY(g1,g8) = 22.0129
    c: Vertical(g0)
    c: Horizontal(g1)
    c: Radius(g2) = 6.2
    c: Coincident(g9,g2)
    c: Radius(g9) = 6.2
    c: DistanceY(g-5,g-4) = 23
    c: Vertical(g4)
    c: Vertical(g6)
    c: Horizontal(g3)
    c: Horizontal(g5)
FEATURE [PartDesign::Pocket] Pocket002
  BaseFeature = -> Pocket001
  Length = 5
  Length2 = 100
  Profile = -> Sketch005
  Type = 0
FEATURE [Sketcher::SketchObject] Sketch006
  AttachmentOffset = pos=(7.7,0,0) rot=(0,0,1;0rad)
  ExternalGeometry = -> [Pocket002]
  MapMode = 5
  Placement = pos=(7.7,0,13.5) rot=(1,0,0;3.14159rad)
  Support = -> [Pocket002]
  sketch-geometry (4):
    g0: LineSegment StartX=-23.85 StartY=15.3 StartZ=0 EndX=8.15 EndY=15.3 EndZ=0
    g1: LineSegment StartX=8.15 StartY=15.3 StartZ=0 EndX=8.15 EndY=-15.3 EndZ=0
    g2: LineSegment StartX=8.15 StartY=-15.3 StartZ=0 EndX=-23.85 EndY=-15.3 EndZ=0
    g3: LineSegment StartX=-23.85 StartY=-15.3 StartZ=0 EndX=-23.85 EndY=15.3 EndZ=0
FEATURE [PartDesign::Pocket] Pocket003
  BaseFeature = -> Pocket002
  Length = 0.7
  Length2 = 100
  Profile = -> Sketch006
  Type = 0
FEATURE [PartDesign::Fillet] Fillet
  Base = -> Pocket003 [Edge38]
  BaseFeature = -> Pocket003
  Radius = 2
FEATURE [PartDesign::Chamfer] Chamfer
  Base = -> Fillet [Edge60,Edge61,Edge62,Edge63]
  BaseFeature = -> Fillet
  Size = 1
FEATURE [Sketcher::SketchObject] Sketch007
  MapMode = 5
  Placement = pos=(0,0,15.5) rot=(0,0,1;0rad)
  sketch-geometry (4):
    g0: Circle CenterX=34.8 CenterY=17.3 CenterZ=0 NormalX=0 NormalY=0 NormalZ=1 AngleXU=0 Radius=2.63102
    g1: Circle CenterX=-34.8 CenterY=17.3 CenterZ=0 NormalX=0 NormalY=0 NormalZ=1 AngleXU=0 Radius=2.66333
    g2: Circle CenterX=-34.8 CenterY=-17.3 CenterZ=0 NormalX=0 NormalY=0 NormalZ=1 AngleXU=0 Radius=2.82775
    g3: Circle CenterX=34.8 CenterY=-17.3 CenterZ=0 NormalX=0 NormalY=0 NormalZ=1 AngleXU=0 Radius=2.89107
FEATURE [PartDesign::Hole] Hole
  BaseFeature = -> Chamfer
  Depth = 20
  DepthType = 1
  Diameter = 3.3
  DrillPoint = 1
  DrillPointAngle = 118
  HoleCutCountersinkAngle = 90
  HoleCutDepth = 0
  HoleCutDiameter = 3
  HoleCutType = 0
  ModelActualThread = false
  Profile = -> Sketch007
  Tapered = false
  TaperedAngle = 90
  ThreadAngle = 60
  ThreadClass = 0
  ThreadCutOffInner = 0.0433013
  ThreadCutOffOuter = 0.0866025
  ThreadDirection = 0
  ThreadFit = 0
  ThreadPitch = 0.4
  ThreadSize = 3
  ThreadType = 1
  Threaded = false
FEATURE [Sketcher::SketchObject] Sketch008
  ExternalGeometry = -> [Hole]
  MapMode = 5
  Placement = pos=(0,0,15.5) rot=(0,0,1;0rad)
  Support = -> [Hole]
  sketch-geometry (4):
    g0: Circle CenterX=34.8 CenterY=17.3 CenterZ=0 NormalX=0 NormalY=0 NormalZ=1 AngleXU=0 Radius=2.8
    g1: Circle CenterX=34.8 CenterY=-17.3 CenterZ=0 NormalX=0 NormalY=0 NormalZ=1 AngleXU=0 Radius=2.8
    g2: Circle CenterX=-34.8 CenterY=-17.3 CenterZ=0 NormalX=0 NormalY=0 NormalZ=1 AngleXU=0 Radius=2.8
    g3: Circle CenterX=-34.8 CenterY=17.3 CenterZ=0 NormalX=0 NormalY=0 NormalZ=1 AngleXU=0 Radius=2.8
  constraints (7):
    c: Coincident(g0,g-5)
    c: Coincident(g1,g-8)
    c: Coincident(g3,g-6)
    c: Radius(g3) = 2.8
    c: Radius(g0) = 2.8
    c: Radius(g2) = 2.8
    c: Radius(g1) = 2.8
FEATURE [PartDesign::Pocket] Pocket004
  BaseFeature = -> Hole
  Length = 3.3
  Length2 = 100
  Profile = -> Sketch008
  Type = 0
FEATURE [Sketcher::SketchObject] Sketch009
  MapMode = 5
  Placement = pos=(0,0,15.5) rot=(0,0,1;0rad)
  Support = -> [Pocket004]
  expr: Constraints[38] = Sketch.Constraints[42]
  expr: Constraints[16] = Sketch.Constraints[20]
  expr: Constraints[17] = Sketch.Constraints[21]
  expr: Constraints[25] = Sketch.Constraints[29]
  expr: Constraints[27] = Sketch.Constraints[31]
  expr: Constraints[26] = Sketch.Constraints[30]
  expr: Constraints[6] = Sketch.Constraints[8]
  expr: Constraints[36] = Sketch.Constraints[40]
  expr: Constraints[7] = Sketch.Constraints[9]
  expr: Constraints[24] = Sketch.Constraints[28]
  expr: Constraints[47] = Sketch.Constraints[51]
  expr: Constraints[39] = Sketch.Constraints[43]
  expr: Constraints[37] = Sketch.Constraints[41]
  expr: Constraints[43] = Sketch.Constraints[47]
  expr: Constraints[45] = Sketch.Constraints[49]
  expr: Constraints[41] = Sketch.Constraints[45]
  sketch-geometry (62):
    g0: LineSegment [constr] StartX=-32.5 StartY=15 StartZ=0 EndX=32.5 EndY=15 EndZ=0
    g1: LineSegment [constr] StartX=32.5 StartY=15 StartZ=0 EndX=32.5 EndY=-15 EndZ=0
    g2: LineSegment [constr] StartX=32.5 StartY=-15 StartZ=0 EndX=-32.5 EndY=-15 EndZ=0
    g3: LineSegment [constr] StartX=-32.5 StartY=-15 StartZ=0 EndX=-32.5 EndY=15 EndZ=0
    g4: LineSegment [constr] StartX=-29 StartY=11.5 StartZ=0 EndX=29 EndY=11.5 EndZ=0
    g5: LineSegment [constr] StartX=29 StartY=11.5 StartZ=0 EndX=29 EndY=-11.5 EndZ=0
    g6: LineSegment [constr] StartX=29 StartY=-11.5 StartZ=0 EndX=-29 EndY=-11.5 EndZ=0
    g7: LineSegment [constr] StartX=-29 StartY=-11.5 StartZ=0 EndX=-29 EndY=11.5 EndZ=0
    g8: Circle [constr] CenterX=-29 CenterY=11.5 CenterZ=0 NormalX=0 NormalY=0 NormalZ=1 AngleXU=0 Radius=1.375
    g9: Circle [constr] CenterX=29 CenterY=11.5 CenterZ=0 NormalX=0 NormalY=0 NormalZ=1 AngleXU=0 Radius=1.375
    g10: Circle [constr] CenterX=29 CenterY=-11.5 CenterZ=0 NormalX=0 NormalY=0 NormalZ=1 AngleXU=0 Radius=1.375
    g11: Circle [constr] CenterX=-29 CenterY=-11.5 CenterZ=0 NormalX=0 NormalY=0 NormalZ=1 AngleXU=0 Radius=1.375
    g12: LineSegment [constr] StartX=-29.5 StartY=12 StartZ=0 EndX=29.5 EndY=12 EndZ=0
    g13: LineSegment [constr] StartX=29.5 StartY=12 StartZ=0 EndX=29.5 EndY=-12 EndZ=0
    g14: LineSegment [constr] StartX=29.5 StartY=-12 StartZ=0 EndX=-29.5 EndY=-12 EndZ=0
    g15: LineSegment [constr] StartX=-29.5 StartY=-12 StartZ=0 EndX=-29.5 EndY=12 EndZ=0
    g16: ArcOfCircle [constr] CenterX=-29.5 CenterY=12 CenterZ=0 NormalX=0 NormalY=0 NormalZ=1 AngleXU=0 Radius=3 StartAngle=1.5708 EndAngle=3.14159
    g17: ArcOfCircle [constr] CenterX=29.5 CenterY=12 CenterZ=0 NormalX=0 NormalY=0 NormalZ=1 AngleXU=0 Radius=3 StartAngle=5.0002e-08 EndAngle=1.5708
    g18: ArcOfCircle [constr] CenterX=29.5 CenterY=-12 CenterZ=0 NormalX=0 NormalY=0 NormalZ=1 AngleXU=0 Radius=3 StartAngle=4.71239 EndAngle=6.28319
    g19: ArcOfCircle [constr] CenterX=-29.5 CenterY=-12 CenterZ=0 NormalX=0 NormalY=0 NormalZ=1 AngleXU=0 Radius=3 StartAngle=3.14159 EndAngle=4.71239
    g20: LineSegment [constr] StartX=-29.5 StartY=15 StartZ=0 EndX=29.5 EndY=15 EndZ=0
    g21: LineSegment [constr] StartX=32.5 StartY=12 StartZ=0 EndX=32.5 EndY=-12 EndZ=0
    g22: LineSegment [constr] StartX=29.5 StartY=-15 StartZ=0 EndX=-29.5 EndY=-15 EndZ=0
    g23: LineSegment [constr] StartX=-32.5 StartY=-12 StartZ=0 EndX=-32.5 EndY=12 EndZ=0
    g24: LineSegment [constr] StartX=25.3417 StartY=8.13712 StartZ=0 EndX=27.8417 EndY=8.13712 EndZ=0
    g25: LineSegment [constr] StartX=27.8417 StartY=8.13712 StartZ=0 EndX=27.8417 EndY=-1.46288 EndZ=0
    g26: LineSegment [constr] StartX=27.8417 StartY=-1.46288 StartZ=0 EndX=25.3417 EndY=-1.46288 EndZ=0
    g27: LineSegment [constr] StartX=25.3417 StartY=-1.46288 StartZ=0 EndX=25.3417 EndY=8.13712 EndZ=0
    g28: LineSegment [constr] StartX=25.3417 StartY=6.93712 StartZ=0 EndX=27.8417 EndY=6.93712 EndZ=0
    g29: LineSegment [constr] StartX=25.3417 StartY=5.73712 StartZ=0 EndX=27.8417 EndY=5.73712 EndZ=0
    g30: LineSegment [constr] StartX=25.3417 StartY=4.53712 StartZ=0 EndX=27.8417 EndY=4.53712 EndZ=0
    g31: LineSegment [constr] StartX=25.3417 StartY=3.33712 StartZ=0 EndX=27.8417 EndY=3.33712 EndZ=0
    g32: LineSegment [constr] StartX=25.3417 StartY=2.13712 StartZ=0 EndX=27.8417 EndY=2.13712 EndZ=0
    g33: LineSegment [constr] StartX=25.3417 StartY=0.937121 StartZ=0 EndX=27.8417 EndY=0.937121 EndZ=0
    g34: LineSegment [constr] StartX=25.3417 StartY=-0.262879 StartZ=0 EndX=27.8417 EndY=-0.262879 EndZ=0
    g35: ArcOfCircle CenterX=25.3417 CenterY=8.13712 CenterZ=0 NormalX=0 NormalY=0 NormalZ=1 AngleXU=0 Radius=0.75 StartAngle=1.12328 EndAngle=4.26487
    g36: ArcOfCircle CenterX=27.8417 CenterY=6.93712 CenterZ=0 NormalX=0 NormalY=0 NormalZ=1 AngleXU=0 Radius=0.75 StartAngle=4.26487 EndAngle=7.40646
    g37: Circle [constr] CenterX=27.8417 CenterY=6.93712 CenterZ=0 NormalX=0 NormalY=0 NormalZ=1 AngleXU=0 Radius=0.75
    g38: Circle [constr] CenterX=25.3417 CenterY=8.13712 CenterZ=0 NormalX=0 NormalY=0 NormalZ=1 AngleXU=0 Radius=0.75
    g39: LineSegment [constr] StartX=25.4338 StartY=8.92483 StartZ=0 EndX=28.7439 EndY=7.33601 EndZ=0
    g40: LineSegment [constr] StartX=24.2457 StartY=7.83129 StartZ=0 EndX=27.5618 EndY=6.23954 EndZ=0
    g41: LineSegment StartX=25.6663 StartY=8.81326 StartZ=0 EndX=28.1663 EndY=7.61326 EndZ=0
    g42: LineSegment StartX=25.0172 StartY=7.46098 StartZ=0 EndX=27.5172 EndY=6.26098 EndZ=0
    g43: ArcOfCircle CenterX=25.3417 CenterY=5.73712 CenterZ=0 NormalX=0 NormalY=0 NormalZ=1 AngleXU=0 Radius=0.75 StartAngle=1.12852 EndAngle=4.25962
    g44: LineSegment StartX=25.6627 StartY=6.41496 StartZ=0 EndX=28.149 EndY=5.22128 EndZ=0
    g45: ArcOfCircle CenterX=27.8417 CenterY=4.53712 CenterZ=0 NormalX=0 NormalY=0 NormalZ=1 AngleXU=0 Radius=0.75 StartAngle=4.23957 EndAngle=7.43184
    g46: LineSegment StartX=25.0136 StartY=5.06269 StartZ=0 EndX=27.5002 EndY=3.86941 EndZ=0
    g47: Circle CenterX=25.3417 CenterY=-1.46288 CenterZ=0 NormalX=0 NormalY=0 NormalZ=1 AngleXU=0 Radius=0.75
    g48: Circle CenterX=27.8417 CenterY=-0.262879 CenterZ=0 NormalX=0 NormalY=0 NormalZ=1 AngleXU=0 Radius=0.75
    g49: Circle CenterX=25.3417 CenterY=0.937121 CenterZ=0 NormalX=0 NormalY=0 NormalZ=1 AngleXU=0 Radius=0.75
    g50: Circle CenterX=27.8417 CenterY=2.13712 CenterZ=0 NormalX=0 NormalY=0 NormalZ=1 AngleXU=0 Radius=0.75
    g51: Circle CenterX=25.3417 CenterY=3.33712 CenterZ=0 NormalX=0 NormalY=0 NormalZ=1 AngleXU=0 Radius=0.75
    g52: LineSegment [constr] StartX=25.8911 StartY=-2.0311 StartZ=0 EndX=28.1814 EndY=-0.931754 EndZ=0
    g53: LineSegment [constr] StartX=24.1632 StartY=-1.19664 StartZ=0 EndX=27.4908 EndY=0.400624 EndZ=0
    g54: LineSegment [constr] StartX=24.363 StartY=0.574977 StartZ=0 EndX=28.2413 EndY=-1.28662 EndZ=0
    g55: LineSegment [constr] StartX=25.6678 StartY=1.61253 StartZ=0 EndX=28.5751 EndY=0.217016 EndZ=0
    g56: LineSegment [constr] StartX=24.9997 StartY=-0.0589725 StartZ=0 EndX=28.6995 EndY=1.71693 EndZ=0
    g57: LineSegment [constr] StartX=24.1511 StartY=1.19754 StartZ=0 EndX=27.2971 EndY=2.70762 EndZ=0
    g58: LineSegment [constr] StartX=24.3738 StartY=2.96979 StartZ=0 EndX=27.5399 EndY=1.45005 EndZ=0
    g59: Circle [constr] CenterX=25.3417 CenterY=2.13712 CenterZ=0 NormalX=0 NormalY=0 NormalZ=1 AngleXU=0 Radius=0.331828
    g60: Circle [constr] CenterX=27.8417 CenterY=0.937121 CenterZ=0 NormalX=0 NormalY=0 NormalZ=1 AngleXU=0 Radius=0.331828
    g61: Circle [constr] CenterX=25.3417 CenterY=-0.262879 CenterZ=0 NormalX=0 NormalY=0 NormalZ=1 AngleXU=0 Radius=0.331828
  constraints (161):
    c: Coincident(g0,g1)
    c: Coincident(g1,g2)
    c: Coincident(g2,g3)
    c: Coincident(g3,g0)
    c: Horizontal(g2)
    c: Vertical(g3)
    c: DistanceX(g0,g0) = 65
    c: DistanceY(g1,g1) = 30
    c: Symmetric(g0,g0,g-2)
    c: Symmetric(g0,g1,g-1)
    c: Coincident(g4,g5)
    c: Coincident(g5,g6)
    c: Coincident(g6,g7)
    c: Coincident(g7,g4)
    c: Horizontal(g6)
    c: Vertical(g7)
    c: DistanceX(g4,g4) = 58
    c: DistanceY(g5,g5) = 23
    c: Symmetric(g4,g5,g-1)
    c: Symmetric(g4,g4,g-2)
    c: Coincident(g8,g4)
    c: Coincident(g9,g4)
    c: Coincident(g10,g5)
    c: Coincident(g11,g6)
    c: Radius(g11) = 1.375
    c: Radius(g8) = 1.375
    c: Radius(g9) = 1.375
    c: Radius(g10) = 1.375
    c: Coincident(g12,g13)
    c: Coincident(g13,g14)
    c: Coincident(g14,g15)
    c: Coincident(g15,g12)
    c: Horizontal(g12)
    c: Horizontal(g14)
    c: Vertical(g13)
    c: Vertical(g15)
    c: DistanceX(g4,g12) = 0.5
    c: DistanceY(g4,g12) = 0.5
    c: DistanceY(g13,g5) = 0.5
    c: DistanceX(g14,g6) = 0.5
    c: Coincident(g16,g12)
    c: Radius(g16) = 3
    c: Coincident(g17,g12)
    c: Radius(g17) = 3
    c: Coincident(g18,g13)
    c: Radius(g18) = 3
    c: Coincident(g19,g14)
    c: Radius(g19) = 3
    c: PointOnObject(g16,g0)
    c: PointOnObject(g17,g1)
    c: PointOnObject(g18,g2)
    c: PointOnObject(g19,g3)
    c: Coincident(g20,g16)
    c: Horizontal(g20)
    c: Coincident(g20,g17)
    c: Coincident(g21,g17)
    c: Vertical(g21)
    c: Coincident(g18,g21)
    c: Coincident(g22,g18)
    c: Horizontal(g22)
    c: Coincident(g19,g22)
    c: Coincident(g23,g19)
    c: Vertical(g23)
    c: Coincident(g23,g16)
    c: Coincident(g24,g25)
    c: Coincident(g25,g26)
    c: Coincident(g26,g27)
    c: Coincident(g27,g24)
    c: Horizontal(g24)
    c: Horizontal(g26)
    c: Vertical(g25)
    c: Vertical(g27)
    c: DistanceX(g4,g24) = 54.3417  '3,362879'
    c: DistanceX(g24,g24) = 2.5
    c: DistanceY(g27,g27) = 9.6
    c: DistanceY(g24,g4) = 3.36288
    c: Horizontal(g28)
    c: Horizontal(g29)
    c: Horizontal(g30)
    c: Horizontal(g32)
    c: Horizontal(g33)
    c: DistanceY(g28,g24) = 1.2
    c: DistanceY(g29,g28) = 1.2
    c: DistanceY(g30,g29) = 1.2
    c: DistanceY(g31,g30) = 1.2
    c: DistanceY(g32,g31) = 1.2
    c: DistanceY(g33,g32) = 1.2
    c: Horizontal(g34)
    c: DistanceY(g34,g33) = 1.2
    c: PointOnObject(g28,g27)
    c: PointOnObject(g29,g27)
    c: PointOnObject(g30,g27)
    c: PointOnObject(g31,g27)
    c: PointOnObject(g32,g27)
    c: PointOnObject(g33,g27)
    c: PointOnObject(g34,g27)
    c: PointOnObject(g34,g25)
    c: PointOnObject(g33,g25)
    c: PointOnObject(g32,g25)
    c: PointOnObject(g31,g25)
    c: PointOnObject(g30,g25)
    c: PointOnObject(g29,g25)
    c: PointOnObject(g28,g25)
    c: Coincident(g35,g24)
    c: Coincident(g36,g28)
    c: Radius(g35) = 0.75
    c: Radius(g36) = 0.75
    c: Coincident(g37,g28)
    c: Coincident(g38,g24)
    c: Radius(g38) = 0.75
    c: Radius(g37) = 0.75
    c: Tangent(g39,g37)
    c: Tangent(g39,g38)
    c: Tangent(g40,g38)
    c: Tangent(g40,g37)
    c: PointOnObject(g41,g39)
    c: PointOnObject(g41,g39)
    c: PointOnObject(g42,g40)
    c: PointOnObject(g42,g40)
    c: Coincident(g41,g35)
    c: Coincident(g35,g42)
    c: Coincident(g41,g36)
    c: Coincident(g36,g42)
    c: Equal(g35,g43) = 0.75
    c: Equal(g36,g45) = 0.75
    c: Coincident(g44,g43)
    c: Coincident(g43,g46)
    c: Coincident(g44,g45)
    c: Coincident(g45,g46)
    c: Coincident(g43,g29)
    c: Coincident(g45,g30)
    c: Coincident(g48,g34)
    c: Coincident(g49,g33)
    c: Coincident(g50,g32)
    c: Coincident(g51,g31)
    c: Radius(g51) = 0.75
    c: Radius(g50) = 0.75
    c: Radius(g49) = 0.75
    c: Radius(g48) = 0.75
    c: Radius(g47) = 0.75
    c: Tangent(g55,g48)
    c: Tangent(g55,g49)
    c: Tangent(g54,g49)
    c: Tangent(g54,g48)
    c: Tangent(g53,g47)
    c: Tangent(g53,g48)
    c: Coincident(g47,g26)
    c: Tangent(g47,g52)
    c: Tangent(g52,g48)
    c: Tangent(g56,g49)
    c: Tangent(g56,g50)
    c: Tangent(g57,g50)
    c: Tangent(g57,g49)
    c: Tangent(g58,g51)
    c: Tangent(g58,g50)
    c: Coincident(g59,g32)
    c: Tangent(g59,g58)
    c: Coincident(g60,g33)
    c: Tangent(g60,g56)
    c: Coincident(g61,g34)
    c: Tangent(g61,g54)
FEATURE [PartDesign::Pocket] Pocket005
  BaseFeature = -> Pocket004
  Length = 5
  Length2 = 100
  Profile = -> Sketch009
  Type = 2
FEATURE [Part::Feature] path76
  shape: bbox 67.53 x 33.36 x 2e-07 mm, 1 faces, 0 solids (baked)
FEATURE [Part::Feature] path76001
  shape: bbox 56.51 x 33.36 x 2e-07 mm, 1 faces, 0 solids (baked)
FEATURE [Part::Feature] path76002
  shape: bbox 67.23 x 33.39 x 2e-07 mm, 1 faces, 0 solids (baked)
FEATURE [Part::Feature] path76003
  shape: bbox 86.8 x 33.05 x 2e-07 mm, 1 faces, 0 solids (baked)
FEATURE [Part::Feature] path76004
  shape: bbox 24.36 x 17.06 x 2e-07 mm, 1 faces, 0 solids (baked)
FEATURE [Part::Cut] Cut
  Base = -> path76003
  Tool = -> path76004
FEATURE [Part::MultiFuse] Fusion
  Shapes = -> [path76,path76001,path76002,Cut]
FEATURE [Part::FeaturePython] Scale001  # Draft clone (typed FeaturePython)
  Fuse = false
  Objects = -> [Fusion]
  Placement = pos=(-20,0,14.85) rot=(0,0,1;0rad)
  Scale = (0.18,0.18,0.18)
FEATURE [Part::FeaturePython] Scale  # Draft clone (typed FeaturePython)
  Fuse = false
  Objects = -> [Scale001]
  Placement = pos=(-11.9,-2.3,14.95) rot=(0,0,1;0rad)
  Scale = (0.8,0.8,0.8)
FEATURE [PartDesign::Fillet] Fillet001
  Base = -> Pocket005 [Edge29,Edge25,Edge20,Edge34,Edge22,Edge21,Edge33,Edge107,Edge99,Edge88,Edge116,Edge92,Edge90,Edge114]
  BaseFeature = -> Pocket005
  Radius = 0.2
FEATURE [PartDesign::Fillet] Fillet002
  Base = -> Fillet001 [Edge30,Edge24,Edge31,Edge25]
  BaseFeature = -> Fillet001
  Radius = 0.1
FEATURE [PartDesign::Fillet] Fillet004
  Base = -> Fillet002 [Edge247,Edge253,Edge252,Edge251,Edge248]
  BaseFeature = -> Fillet002
  Radius = 0.1
FEATURE [PartDesign::Body] Body
  Group = -> [Sketch,Sketch001,Pad,Sketch002,Pocket,Sketch003,Pocket001,Sketch004,Sketch005,Pocket002,Sketch006,Pocket003,Fillet,Chamfer,Sketch007,Hole,Sketch008,Pocket004,Sketch009,Pocket005,Fillet001,Fillet002,Fillet004]
  Origin = -> Origin
  Tip = -> Fillet004
FEATURE [Part::Extrusion] Extrude
  Base = -> Scale
  Dir = (0,0,1)
  DirMode = 0
  FaceMakerClass = Part::FaceMakerBullseye
  LengthFwd = 5
  LengthRev = 0
  Solid = false
  Symmetric = false
FEATURE [Part::Cut] Cut001
  Base = -> Fillet004
  Tool = -> Extrude
FEATURE [Mesh::Feature] Mesh  label="Cut001 (Meshed)"
